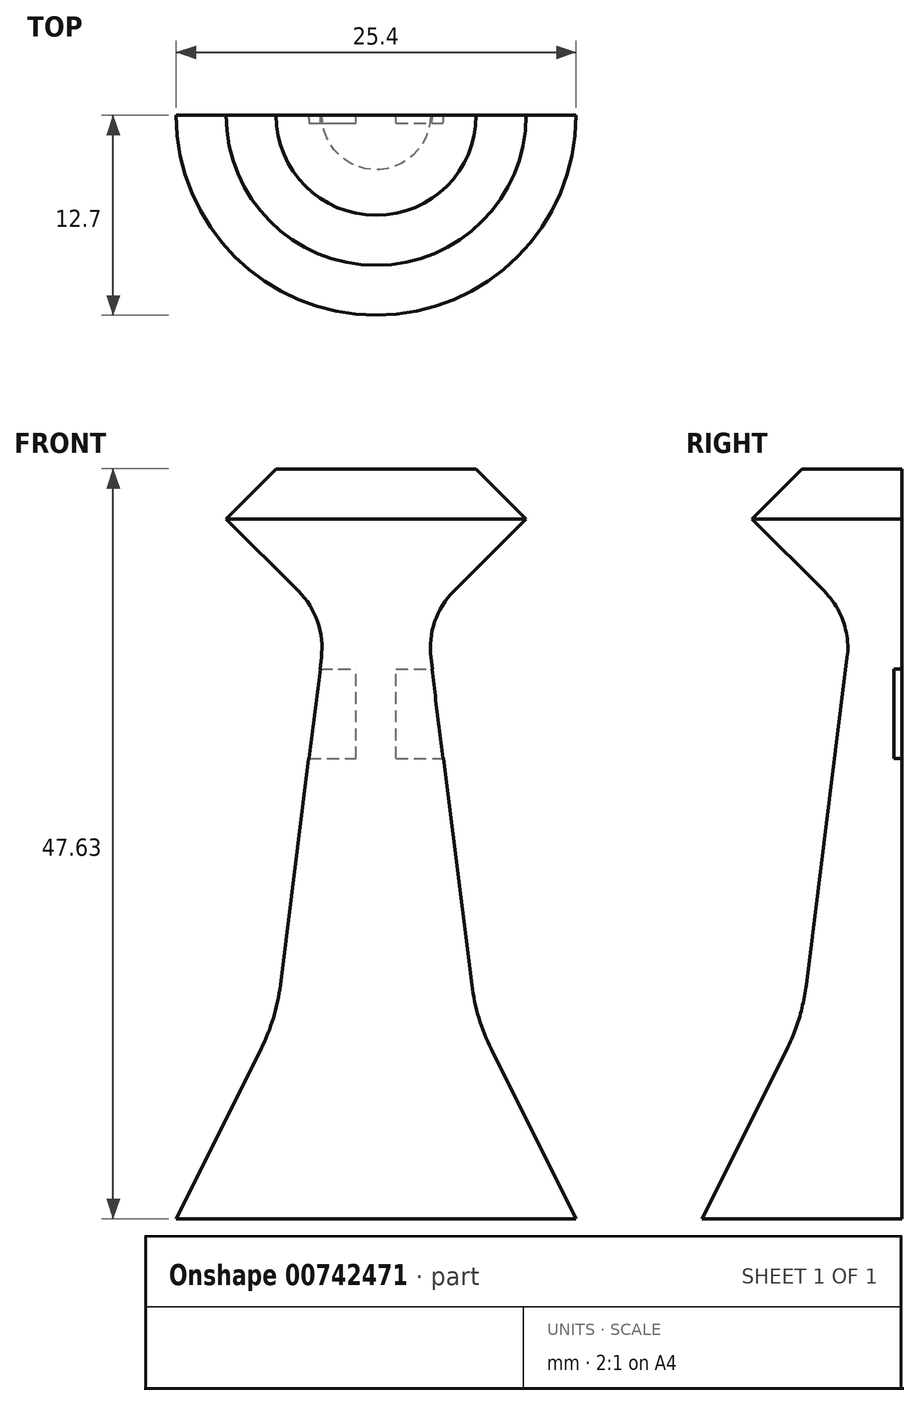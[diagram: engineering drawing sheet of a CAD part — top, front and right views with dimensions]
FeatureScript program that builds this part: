
annotation { "Feature Type Name" : "Feature", "Feature Type Description" : "" }
export const myFeature = defineFeature(function(context is Context, id is Id, definition is map)
    precondition{}
    {
        {
            var Q0;
            Q0=qCreatedBy(makeId("Top.planeOp"),FACE);
            var sketch = newSketch(context, id + "F0", { "sketchPlane" : qUnion([Q0])});
            skCircle(sketch, "E0", {"center": v(0, 0) * mm, "radius": 12.7 * mm});
            skSolve(sketch);
        }
        {
            var Q0;
            Q0=qCreatedBy(makeId("Top.planeOp"),FACE);
            cPlane(context, id + "F1", {"entities" : qUnion([Q0]), "cplaneType" : CPlaneType.OFFSET, "offset" : 12.7 * mm, "width" : 152.4 * mm, "height" : 152.4 * mm});
        }
        {
            var Q0;
            Q0=qCreatedBy(id+"F1.planeOp",FACE);
            var sketch = newSketch(context, id + "F2", { "sketchPlane" : qUnion([Q0])});
            skCircle(sketch, "E1", {"center": v(0, 0) * mm, "radius": 6.35 * mm});
            skSolve(sketch);
        }
        {
            var Q0;
            Q0=makeQuery(id+"F0.imprint","IMPRINT",FACE,{"disambiguationData":[TD([[makeQuery(id+"F0.imprint","IMPRINT",EDGE,{"derivedFrom":sQuery(id+"F0.wireOp",EDGE,"E0")}),1.0]])]});
            var Q1;
            Q1=makeQuery(id+"F2.imprint","IMPRINT",FACE,{"disambiguationData":[TD([[makeQuery(id+"F2.imprint","IMPRINT",EDGE,{"derivedFrom":sQuery(id+"F2.wireOp",EDGE,"E1")}),1.0]])]});
            loft(context, id + "F3", {"sheetProfilesArray" : [{ "sheetProfileEntities" : qUnion([Q0]) }, { "sheetProfileEntities" : qUnion([Q1]) }]});
        }
        {
            var Q0;
            Q0=qCreatedBy(makeId("Top.planeOp"),FACE);
            cPlane(context, id + "F4", {"entities" : qUnion([Q0]), "cplaneType" : CPlaneType.OFFSET, "offset" : 38.1 * mm, "width" : 152.4 * mm, "height" : 152.4 * mm});
        }
        {
            var Q0;
            Q0=qCreatedBy(id+"F4.planeOp",FACE);
            var sketch = newSketch(context, id + "F5", { "sketchPlane" : qUnion([Q0])});
            skCircle(sketch, "E2", {"center": v(0, 0) * mm, "radius": 3.18 * mm});
            skSolve(sketch);
        }
        {
            var Q1;
            Q1=makeQuery(id+"F3.opLoft","CAP_FACE",FACE,{"disambiguationData":[OSD([makeQuery(id+"F2.imprint","IMPRINT",FACE,{"disambiguationData":[TD([[makeQuery(id+"F2.imprint","IMPRINT",EDGE,{"derivedFrom":sQuery(id+"F2.wireOp",EDGE,"E1")}),1.0]])]})])],"isStart":true});
            var Q2;
            Q2=makeQuery(id+"F5.imprint","IMPRINT",FACE,{"disambiguationData":[TD([[makeQuery(id+"F5.imprint","IMPRINT",EDGE,{"derivedFrom":sQuery(id+"F5.wireOp",EDGE,"E2")}),1.0]])]});
            loft(context, id + "F6", {"operationType" : NewBodyOperationType.ADD, "sheetProfilesArray" : [{ "sheetProfileEntities" : qUnion([Q1]) }, { "sheetProfileEntities" : qUnion([Q2]) }]});
        }
        {
            var Q0;
            Q0=qCreatedBy(makeId("Top.planeOp"),FACE);
            cPlane(context, id + "F7", {"entities" : qUnion([Q0]), "cplaneType" : CPlaneType.OFFSET, "offset" : 44.45 * mm, "width" : 152.4 * mm, "height" : 152.4 * mm});
        }
        {
            var Q0;
            Q0=qCreatedBy(id+"F7.planeOp",FACE);
            var sketch = newSketch(context, id + "F8", { "sketchPlane" : qUnion([Q0])});
            skCircle(sketch, "E3", {"center": v(0, 0) * mm, "radius": 9.53 * mm});
            skSolve(sketch);
        }
        {
            var Q1;
            Q1=makeQuery(id+"F6.opLoft","CAP_FACE",FACE,{"disambiguationData":[OSD([makeQuery(id+"F5.imprint","IMPRINT",FACE,{"disambiguationData":[TD([[makeQuery(id+"F5.imprint","IMPRINT",EDGE,{"derivedFrom":sQuery(id+"F5.wireOp",EDGE,"E2")}),1.0]])]})])],"isStart":true});
            var Q2;
            Q2=makeQuery(id+"F8.imprint","IMPRINT",FACE,{"disambiguationData":[TD([[makeQuery(id+"F8.imprint","IMPRINT",EDGE,{"derivedFrom":sQuery(id+"F8.wireOp",EDGE,"E3")}),1.0]])]});
            loft(context, id + "F9", {"operationType" : NewBodyOperationType.ADD, "sheetProfilesArray" : [{ "sheetProfileEntities" : qUnion([Q1]) }, { "sheetProfileEntities" : qUnion([Q2]) }]});
        }
        {
            var Q0;
            {var subQ0=sQuery(id+"F2.wireOp",EDGE,"E1");var subQ1=sQuery(id+"F0.wireOp",EDGE,"E0");Q0=makeQuery(id+"F6.boolean.opBoolean","MERGE",EDGE,{"derivedFrom":[makeQuery(id+"F3.opLoft","MID_CAP_EDGE",EDGE,{"disambiguationData":[OSD([subQ1,subQ0])],"capPos":1.0}),makeQuery(id+"F6.opLoft","MID_CAP_EDGE",EDGE,{"disambiguationData":[OSD([subQ1,subQ0])],"capPos":0.0})]});}
            fillet(context, id + "F10", {"entities" : qUnion([Q0]), "radius" : 12.7 * mm, "tangentPropagation" : true, "allowEdgeOverflow" : false});
        }
        {
            var Q0;
            {var subQ0=sQuery(id+"F5.wireOp",EDGE,"E2");var subQ1=sQuery(id+"F2.wireOp",EDGE,"E1");var subQ2=sQuery(id+"F0.wireOp",EDGE,"E0");Q0=makeQuery(id+"F9.boolean.opBoolean","MERGE",EDGE,{"derivedFrom":[makeQuery(id+"F6.opLoft","MID_CAP_EDGE",EDGE,{"disambiguationData":[OSD([subQ2,subQ1,subQ0])],"capPos":1.0}),makeQuery(id+"F9.opLoft","MID_CAP_EDGE",EDGE,{"disambiguationData":[OSD([subQ2,subQ1,subQ0])],"capPos":0.0})]});}
            fillet(context, id + "F11", {"entities" : qUnion([Q0]), "radius" : 5.08 * mm, "tangentPropagation" : true, "allowEdgeOverflow" : false});
        }
        {
            var Q0;
            Q0=qCreatedBy(makeId("Top.planeOp"),FACE);
            cPlane(context, id + "F12", {"entities" : qUnion([Q0]), "cplaneType" : CPlaneType.OFFSET, "offset" : 46.04 * mm, "width" : 152.4 * mm, "height" : 152.4 * mm});
        }
        {
            var Q0;
            Q0=qCreatedBy(id+"F12.planeOp",FACE);
            var sketch = newSketch(context, id + "F13", { "sketchPlane" : qUnion([Q0])});
            skCircle(sketch, "E4", {"center": v(0, 0) * mm, "radius": 7.94 * mm});
            skSolve(sketch);
        }
        {
            var Q1;
            Q1=makeQuery(id+"F9.opLoft","CAP_FACE",FACE,{"disambiguationData":[OSD([makeQuery(id+"F8.imprint","IMPRINT",FACE,{"disambiguationData":[TD([[makeQuery(id+"F8.imprint","IMPRINT",EDGE,{"derivedFrom":sQuery(id+"F8.wireOp",EDGE,"E3")}),1.0]])]})])],"isStart":true});
            var Q2;
            Q2=makeQuery(id+"F13.imprint","IMPRINT",FACE,{"disambiguationData":[TD([[makeQuery(id+"F13.imprint","IMPRINT",EDGE,{"derivedFrom":sQuery(id+"F13.wireOp",EDGE,"E4")}),1.0]])]});
            loft(context, id + "F14", {"operationType" : NewBodyOperationType.ADD, "sheetProfilesArray" : [{ "sheetProfileEntities" : qUnion([Q1]) }, { "sheetProfileEntities" : qUnion([Q2]) }]});
        }
        {
            var Q0;
            Q0=makeQuery(id+"F14.opLoft","CAP_FACE",FACE,{"disambiguationData":[OSD([makeQuery(id+"F13.imprint","IMPRINT",FACE,{"disambiguationData":[TD([[makeQuery(id+"F13.imprint","IMPRINT",EDGE,{"derivedFrom":sQuery(id+"F13.wireOp",EDGE,"E4")}),1.0]])]})])],"isStart":true});
            cPlane(context, id + "F15", {"entities" : qUnion([Q0]), "cplaneType" : CPlaneType.OFFSET, "offset" : 1.59 * mm, "width" : 152.4 * mm, "height" : 152.4 * mm});
        }
        {
            var Q0;
            Q0=qCreatedBy(id+"F15.planeOp",FACE);
            var sketch = newSketch(context, id + "F16", { "sketchPlane" : qUnion([Q0])});
            skCircle(sketch, "E5", {"center": v(0, 0) * mm, "radius": 6.35 * mm});
            skSolve(sketch);
        }
        {
            var Q1;
            Q1=makeQuery(id+"F16.imprint","IMPRINT",FACE,{"disambiguationData":[TD([[makeQuery(id+"F16.imprint","IMPRINT",EDGE,{"derivedFrom":sQuery(id+"F16.wireOp",EDGE,"E5")}),1.0]])]});
            var Q2;
            Q2=makeQuery(id+"F14.opLoft","CAP_FACE",FACE,{"disambiguationData":[OSD([makeQuery(id+"F13.imprint","IMPRINT",FACE,{"disambiguationData":[TD([[makeQuery(id+"F13.imprint","IMPRINT",EDGE,{"derivedFrom":sQuery(id+"F13.wireOp",EDGE,"E4")}),1.0]])]})])],"isStart":true});
            loft(context, id + "F17", {"operationType" : NewBodyOperationType.ADD, "sheetProfilesArray" : [{ "sheetProfileEntities" : qUnion([Q1]) }, { "sheetProfileEntities" : qUnion([Q2]) }]});
        }
        {
            var Q0;
            Q0=qCreatedBy(makeId("Right.planeOp"),FACE);
            var sketch = newSketch(context, id + "F18", { "sketchPlane" : qUnion([Q0])});
            skLineSegment(sketch, "E6", {"start": v(0, 0) * mm, "end": v(0, 30.16) * mm, "construction": true});
            skLineSegment(sketch, "E7", {"start": v(0, 30.16) * mm, "end": v(0, 34.93) * mm, "construction": true});
            skLineSegment(sketch, "E8.bottom", {"start": v(0, 34.93) * mm, "end": v(0.5, 34.93) * mm});
            skLineSegment(sketch, "E8.top", {"start": v(0, 29.24) * mm, "end": v(0.5, 29.24) * mm});
            skLineSegment(sketch, "E8.left", {"start": v(0, 34.93) * mm, "end": v(0, 29.24) * mm});
            skLineSegment(sketch, "E8.right", {"start": v(0.5, 34.93) * mm, "end": v(0.5, 29.24) * mm});
            skLineSegment(sketch, "E9.bottom", {"start": v(0, 34.93) * mm, "end": v(-0.5, 34.93) * mm});
            skLineSegment(sketch, "E9.top", {"start": v(0, 29.24) * mm, "end": v(-0.5, 29.24) * mm});
            skLineSegment(sketch, "E9.right", {"start": v(-0.5, 34.93) * mm, "end": v(-0.5, 29.24) * mm});
            skSolve(sketch);
        }
        {
            var Q0;
            Q0=qSketchRegion(id+"F18",true);
            extrude(context, id + "F19", {"entities" : qUnion([Q0]), "operationType" : NewBodyOperationType.REMOVE, "endBound" : BoundingType.THROUGH_ALL, "oppositeDirection" : true, "depth" : 25.4 * mm, "offsetDistance" : 25.4 * mm, "hasSecondDirection" : true, "secondDirectionOppositeDirection" : false, "secondDirectionDepth" : 25.4 * mm});
        }
        {
            var Q0;
            Q0=qSketchRegion(id+"F18",true);
            extrude(context, id + "F20", {"entities" : qUnion([Q0]), "operationType" : NewBodyOperationType.ADD, "endBound" : BoundingType.SYMMETRIC, "depth" : 2.54 * mm, "offsetDistance" : 25.4 * mm});
        }
        {
            var Q0;
            Q0=qCreatedBy(makeId("Right.planeOp"),FACE);
            var sketch = newSketch(context, id + "F21", { "sketchPlane" : qUnion([Q0])});
            skLineSegment(sketch, "E10.bottom", {"start": v(0, 0) * mm, "end": v(25.07, 0) * mm});
            skLineSegment(sketch, "E10.top", {"start": v(0, 55.59) * mm, "end": v(25.07, 55.59) * mm});
            skLineSegment(sketch, "E10.left", {"start": v(0, 0) * mm, "end": v(0, 55.59) * mm});
            skLineSegment(sketch, "E10.right", {"start": v(25.07, 0) * mm, "end": v(25.07, 55.59) * mm});
            skSolve(sketch);
        }
        {
            var Q0;
            Q0=makeQuery(id+"F21.imprint","IMPRINT",FACE,{"disambiguationData":[TD([[makeQuery(id+"F21.imprint","IMPRINT",EDGE,{"derivedFrom":sQuery(id+"F21.wireOp",EDGE,"E10.bottom")}),1.0]])]});
            extrude(context, id + "F22", {"entities" : qUnion([Q0]), "operationType" : NewBodyOperationType.REMOVE, "endBound" : BoundingType.SYMMETRIC, "oppositeDirection" : true, "depth" : 254 * mm, "offsetDistance" : 25.4 * mm});
        }
    });
